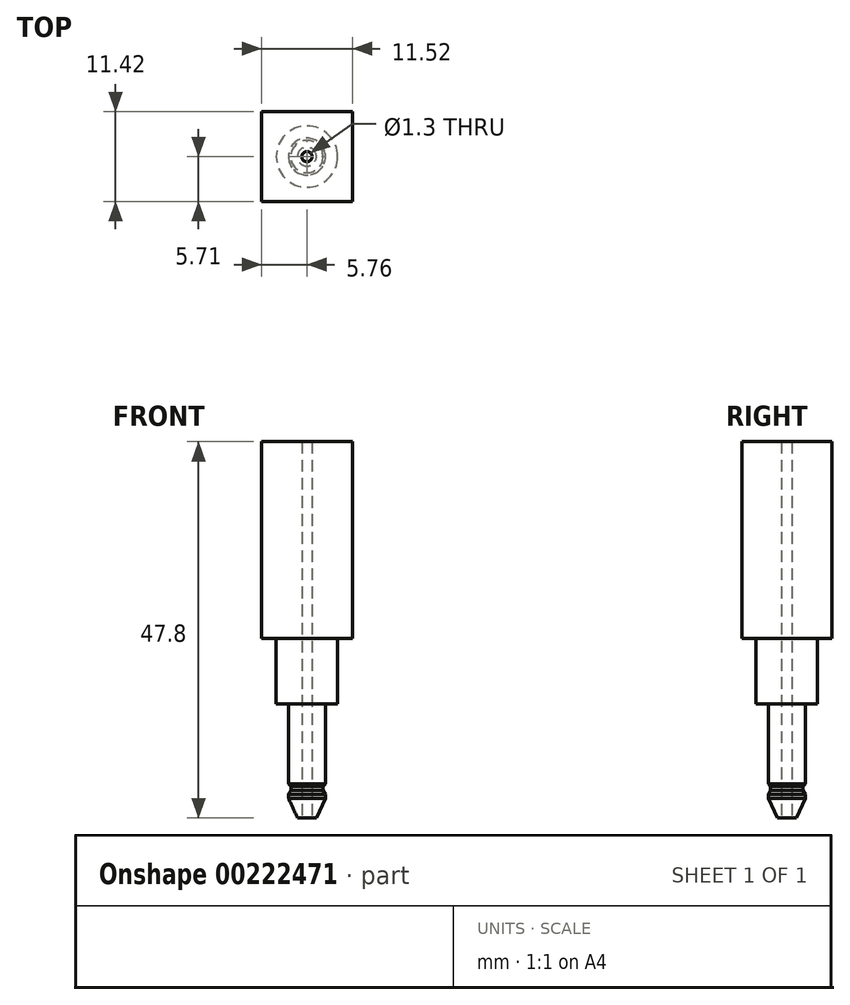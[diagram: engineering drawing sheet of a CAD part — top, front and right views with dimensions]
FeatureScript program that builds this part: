
annotation { "Feature Type Name" : "Feature", "Feature Type Description" : "" }
export const myFeature = defineFeature(function(context is Context, id is Id, definition is map)
    precondition{}
    {
        {
            var Q0;
            Q0=qCreatedBy(makeId("Front.planeOp"),FACE);
            var sketch = newSketch(context, id + "F0", { "sketchPlane" : qUnion([Q0])});
            skLineSegment(sketch, "E0.bottom", {"start": v(-3.9, 11.4) * mm, "end": v(3.9, 11.4) * mm});
            skLineSegment(sketch, "E0.top", {"start": v(-3.9, 3.1) * mm, "end": v(3.9, 3.1) * mm});
            skLineSegment(sketch, "E0.left", {"start": v(-3.9, 11.4) * mm, "end": v(-3.9, 3.1) * mm});
            skLineSegment(sketch, "E0.right", {"start": v(3.9, 11.4) * mm, "end": v(3.9, 3.1) * mm});
            skLineSegment(sketch, "E1.bottom", {"start": v(-2.35, 3.1) * mm, "end": v(2.35, 3.1) * mm});
            skLineSegment(sketch, "E1.top", {"start": v(-2.35, -11.4) * mm, "end": v(2.35, -11.4) * mm});
            skLineSegment(sketch, "E1.left", {"start": v(2.35, 3.1) * mm, "end": v(2.35, -11.4) * mm});
            skLineSegment(sketch, "E1.right", {"start": v(-2.35, 3.1) * mm, "end": v(-2.35, -11.4) * mm});
            skLineSegment(sketch, "E2", {"start": v(0, 11.4) * mm, "end": v(0, -11.4) * mm});
            skSolve(sketch);
        }
        {
            var Q0;
            {var subQ5=sQuery(id+"F0.wireOp",EDGE,"E0.right");Q0=makeQuery(id+"F0.imprint","IMPRINT",FACE,{"disambiguationData":[TD([[makeQuery(id+"F0.imprint","IMPRINT",EDGE,{"derivedFrom":subQ5}),-1.0]])]});}
            var Q1;
            {var subQ0=sQuery(id+"F0.wireOp",EDGE,"E1.left");Q1=makeQuery(id+"F0.imprint","IMPRINT",FACE,{"disambiguationData":[TD([[makeQuery(id+"F0.imprint","IMPRINT",EDGE,{"derivedFrom":subQ0}),-1.0]])]});}
            var Q2;
            Q2=sQuery(id+"F0.wireOp",EDGE,"E2");
            revolve(context, id + "F1", {"entities" : qUnion([Q0, Q1]), "axis" : qUnion([Q2]), "revolveType" : RevolveType.FULL});
        }
        {
            var Q0;
            Q0=qCreatedBy(makeId("Front.planeOp"),FACE);
            var sketch = newSketch(context, id + "F2", { "sketchPlane" : qUnion([Q0])});
            skLineSegment(sketch, "E3", {"start": v(1.2, -11.4) * mm, "end": v(2.35, -8.9) * mm});
            skLineSegment(sketch, "E4", {"start": v(2.35, -8.9) * mm, "end": v(2.35, -8.4) * mm});
            skLineSegment(sketch, "E5", {"start": v(2.35, -8.4) * mm, "end": v(2.05, -7.9) * mm});
            skLineSegment(sketch, "E6", {"start": v(2.05, -7.9) * mm, "end": v(2.05, -7.4) * mm});
            skLineSegment(sketch, "E7", {"start": v(2.05, -7.4) * mm, "end": v(2.35, -7.05) * mm});
            skLineSegment(sketch, "E8", {"start": v(2.35, -7.05) * mm, "end": v(0, -7.05) * mm});
            skLineSegment(sketch, "E9", {"start": v(0, -7.05) * mm, "end": v(0, -11.4) * mm, "construction": true});
            skLineSegment(sketch, "E10", {"start": v(0, -11.4) * mm, "end": v(1.2, -11.4) * mm});
            skLineSegment(sketch, "E11", {"start": v(2.35, -7.05) * mm, "end": v(2.35, -8.4) * mm});
            skLineSegment(sketch, "E12", {"start": v(2.35, -8.9) * mm, "end": v(2.35, -11.4) * mm});
            skLineSegment(sketch, "E13", {"start": v(2.35, -11.4) * mm, "end": v(1.2, -11.4) * mm});
            skSolve(sketch);
        }
        {
            var Q0;
            Q0 = qSketchRegion(id + "F2", true);
            var Q1;
            Q1=sQuery(id+"F0.wireOp",EDGE,"E2");
            revolve(context, id + "F3", {"operationType" : NewBodyOperationType.REMOVE, "entities" : qUnion([Q0]), "axis" : qUnion([Q1]), "revolveType" : RevolveType.FULL, "oppositeDirection" : true});
        }
        {
            var Q0;
            Q0=makeQuery(id+"F1.opRevolve","SWEPT_FACE",FACE,{"disambiguationData":[OSD([sQuery(id+"F0.wireOp",EDGE,"E1.top")])]});
            var sketch = newSketch(context, id + "F4", { "sketchPlane" : qUnion([Q0])});
            skCircle(sketch, "E14", {"center": v(0, 0) * mm, "radius": 0.65 * mm});
            skSolve(sketch);
        }
        {
            var Q0;
            Q0=makeQuery(id+"F4.imprint","IMPRINT",FACE,{"disambiguationData":[TD([[makeQuery(id+"F4.imprint","IMPRINT",EDGE,{"derivedFrom":sQuery(id+"F4.wireOp",EDGE,"E14")}),1.0]])]});
            extrude(context, id + "F5", {"entities" : qUnion([Q0]), "operationType" : NewBodyOperationType.REMOVE, "endBound" : BoundingType.THROUGH_ALL, "oppositeDirection" : true, "depth" : 25 * mm});
        }
        {
            var Q0;
            Q0=makeQuery(id+"F1.opRevolve","SWEPT_FACE",FACE,{"disambiguationData":[OSD([sQuery(id+"F0.wireOp",EDGE,"E0.bottom")])]});
            var sketch = newSketch(context, id + "F6", { "sketchPlane" : qUnion([Q0])});
            skLineSegment(sketch, "E15.bottom", {"start": v(5.76, -5.7) * mm, "end": v(-5.76, -5.7) * mm});
            skLineSegment(sketch, "E15.top", {"start": v(5.76, 5.7) * mm, "end": v(-5.76, 5.7) * mm});
            skLineSegment(sketch, "E15.left", {"start": v(5.76, -5.7) * mm, "end": v(5.76, 5.7) * mm});
            skLineSegment(sketch, "E15.right", {"start": v(-5.76, -5.7) * mm, "end": v(-5.76, 5.7) * mm});
            skPoint(sketch, "E15.middle", {"position": v(0, 0) * mm});
            skSolve(sketch);
        }
        {
            var Q0;
            Q0=makeQuery(id+"F6.imprint","IMPRINT",FACE,{"disambiguationData":[TD([[makeQuery(id+"F6.imprint","IMPRINT",EDGE,{"derivedFrom":sQuery(id+"F6.wireOp",EDGE,"E15.bottom")}),-1.0]])]});
            var Q1;
            {var subQ0=sQuery(id+"F0.wireOp",EDGE,"E0.bottom");Q1=makeQuery(id+"F6.imprint","IMPRINT",FACE,{"disambiguationData":[TD([[makeQuery(id+"F6.imprint","IMPRINT",EDGE,{"derivedFrom":makeQuery(id+"F1.opRevolve","SWEPT_EDGE",EDGE,{"disambiguationData":[OSD([subQ0,sQuery(id+"F0.wireOp",EDGE,"E0.right")])]})}),1.0]])]});}
            extrude(context, id + "F7", {"entities" : qUnion([Q0, Q1]), "operationType" : NewBodyOperationType.ADD, "depth" : 25 * mm});
        }
    });
